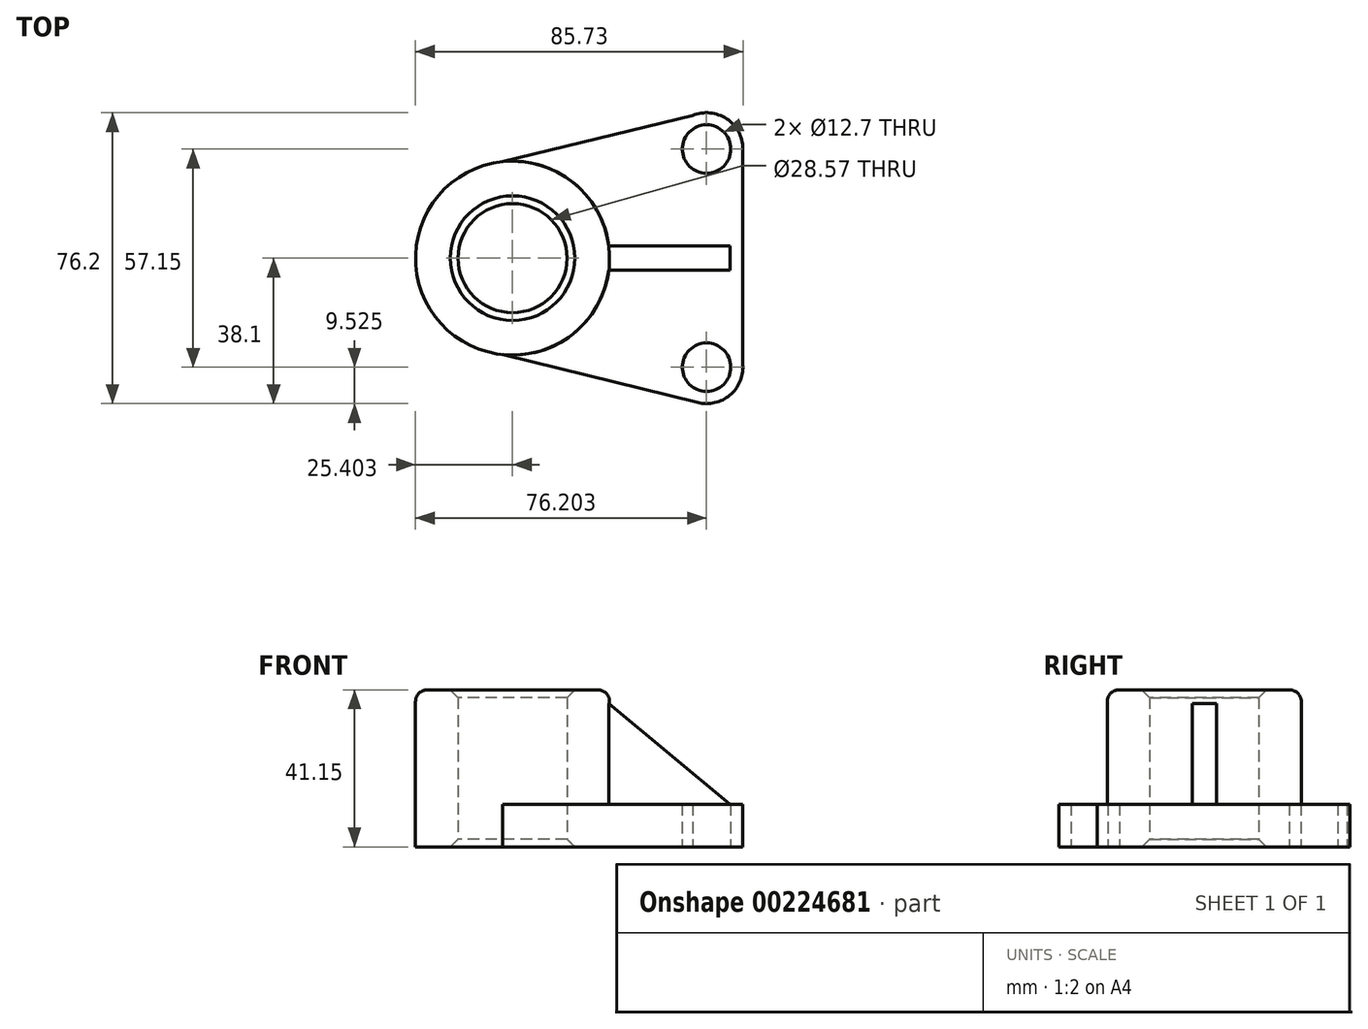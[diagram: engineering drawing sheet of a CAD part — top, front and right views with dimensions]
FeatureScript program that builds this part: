
annotation { "Feature Type Name" : "Feature", "Feature Type Description" : "" }
export const myFeature = defineFeature(function(context is Context, id is Id, definition is map)
    precondition{}
    {
        {
            var Q0;
            Q0=qCreatedBy(makeId("Top.planeOp"),FACE);
            var sketch = newSketch(context, id + "F0", { "sketchPlane" : qUnion([Q0])});
            skCircle(sketch, "E0", {"center": v(-42.43, 0) * mm, "radius": 25.4 * mm});
            skCircle(sketch, "E1", {"center": v(-42.43, 0) * mm, "radius": 14.29 * mm});
            skCircle(sketch, "E2", {"center": v(8.37, 28.58) * mm, "radius": 6.35 * mm});
            skCircle(sketch, "E3", {"center": v(8.37, -28.58) * mm, "radius": 6.35 * mm});
            skCircle(sketch, "E4", {"center": v(8.37, 28.58) * mm, "radius": 9.53 * mm});
            skCircle(sketch, "E5", {"center": v(8.37, -28.58) * mm, "radius": 9.53 * mm});
            skLineSegment(sketch, "E6", {"start": v(4.69, 37.36) * mm, "end": v(-45, 25.27) * mm});
            skLineSegment(sketch, "E7", {"start": v(17.88, -28.04) * mm, "end": v(17.9, 28.58) * mm});
            skLineSegment(sketch, "E8", {"start": v(-45, -25.27) * mm, "end": v(6.1, -37.82) * mm});
            skLineSegment(sketch, "E9.bottom", {"start": v(14.59, -3.18) * mm, "end": v(-23.83, -3.18) * mm});
            skLineSegment(sketch, "E9.top", {"start": v(14.59, 3.18) * mm, "end": v(-23.83, 3.18) * mm});
            skLineSegment(sketch, "E9.left", {"start": v(14.59, -3.18) * mm, "end": v(14.59, 3.18) * mm});
            skLineSegment(sketch, "E9.right", {"start": v(-23.83, -3.18) * mm, "end": v(-23.83, 3.18) * mm});
            skPoint(sketch, "E9.middle", {"position": v(-4.62, 0) * mm});
            skSolve(sketch);
        }
        {
            var Q0;
            Q0=makeQuery(id+"F0.imprint","IMPRINT",FACE,{"disambiguationData":[TD([[makeQuery(id+"F0.imprint","IMPRINT",EDGE,{"derivedFrom":sQuery(id+"F0.wireOp",EDGE,"E1")}),-1.0]])]});
            var Q1;
            {var subQ5=sQuery(id+"F0.wireOp",EDGE,"E9.right");Q1=makeQuery(id+"F0.imprint","IMPRINT",FACE,{"disambiguationData":[TD([[makeQuery(id+"F0.imprint","IMPRINT",EDGE,{"derivedFrom":subQ5}),-1.0]])]});}
            extrude(context, id + "F1", {"entities" : qUnion([Q0, Q1]), "depth" : 41.15 * mm});
        }
        {
            var Q0;
            {var subQ6=sQuery(id+"F0.wireOp",EDGE,"E6");Q0=makeQuery(id+"F0.imprint","IMPRINT",FACE,{"disambiguationData":[TD([[makeQuery(id+"F0.imprint","IMPRINT",EDGE,{"derivedFrom":subQ6}),1.0]])]});}
            var Q1;
            Q1=makeQuery(id+"F0.imprint","IMPRINT",FACE,{"disambiguationData":[TD([[makeQuery(id+"F0.imprint","IMPRINT",EDGE,{"derivedFrom":sQuery(id+"F0.wireOp",EDGE,"E2")}),1.0]])]});
            var Q2;
            Q2=makeQuery(id+"F0.imprint","IMPRINT",FACE,{"disambiguationData":[TD([[makeQuery(id+"F0.imprint","IMPRINT",EDGE,{"derivedFrom":sQuery(id+"F0.wireOp",EDGE,"E3")}),1.0]])]});
            var Q3;
            Q3=makeQuery(id+"F0.imprint","IMPRINT",FACE,{"disambiguationData":[TD([[makeQuery(id+"F0.imprint","IMPRINT",EDGE,{"derivedFrom":sQuery(id+"F0.wireOp",EDGE,"E3")}),-1.0]])]});
            var Q4;
            Q4=makeQuery(id+"F0.imprint","IMPRINT",FACE,{"disambiguationData":[TD([[makeQuery(id+"F0.imprint","IMPRINT",EDGE,{"derivedFrom":sQuery(id+"F0.wireOp",EDGE,"E2")}),-1.0]])]});
            var Q5;
            {var subQ5=sQuery(id+"F0.wireOp",EDGE,"E9.left");Q5=makeQuery(id+"F0.imprint","IMPRINT",FACE,{"disambiguationData":[TD([[makeQuery(id+"F0.imprint","IMPRINT",EDGE,{"derivedFrom":subQ5}),1.0]])]});}
            var Q6;
            {var subQ5=sQuery(id+"F0.wireOp",EDGE,"E9.right");Q6=makeQuery(id+"F0.imprint","IMPRINT",FACE,{"disambiguationData":[TD([[makeQuery(id+"F0.imprint","IMPRINT",EDGE,{"derivedFrom":subQ5}),-1.0]])]});}
            extrude(context, id + "F2", {"entities" : qUnion([Q0, Q1, Q2, Q3, Q4, Q5, Q6]), "operationType" : NewBodyOperationType.ADD, "depth" : 11.18 * mm});
        }
        {
            var Q0;
            {var subQ5=sQuery(id+"F0.wireOp",EDGE,"E9.left");Q0=makeQuery(id+"F0.imprint","IMPRINT",FACE,{"disambiguationData":[TD([[makeQuery(id+"F0.imprint","IMPRINT",EDGE,{"derivedFrom":subQ5}),1.0]])]});}
            extrude(context, id + "F3", {"entities" : qUnion([Q0]), "operationType" : NewBodyOperationType.ADD, "depth" : 37.6 * mm});
        }
        {
            var Q0;
            Q0=makeQuery(id+"F3.opExtrude","SWEPT_FACE",FACE,{"disambiguationData":[OSD([sQuery(id+"F0.wireOp",EDGE,"E9.bottom")])]});
            var sketch = newSketch(context, id + "F4", { "sketchPlane" : qUnion([Q0])});
            skLineSegment(sketch, "E10", {"start": v(-17.23, 37.6) * mm, "end": v(14.59, 11.18) * mm});
            skSolve(sketch);
        }
        {
            var Q0;
            Q0 = qSketchRegion(id + "F4", true);
            var Q1;
            Q1=makeQuery(id+"F4.imprint","IMPRINT",FACE,{"disambiguationData":[TD([[makeQuery(id+"F4.imprint","IMPRINT",EDGE,{"derivedFrom":sQuery(id+"F4.wireOp",EDGE,"E10")}),1.0]])]});
            extrude(context, id + "F5", {"entities" : qUnion([Q0, Q1]), "operationType" : NewBodyOperationType.REMOVE, "oppositeDirection" : true, "depth" : 127 * mm});
        }
        {
            var Q0;
            Q0=makeQuery(id+"F0.imprint","IMPRINT",FACE,{"disambiguationData":[TD([[makeQuery(id+"F0.imprint","IMPRINT",EDGE,{"derivedFrom":sQuery(id+"F0.wireOp",EDGE,"E2")}),1.0]])]});
            var Q1;
            Q1=makeQuery(id+"F0.imprint","IMPRINT",FACE,{"disambiguationData":[TD([[makeQuery(id+"F0.imprint","IMPRINT",EDGE,{"derivedFrom":sQuery(id+"F0.wireOp",EDGE,"E3")}),1.0]])]});
            extrude(context, id + "F6", {"entities" : qUnion([Q0, Q1]), "operationType" : NewBodyOperationType.REMOVE, "depth" : 76.2 * mm});
        }
        {
            var Q0;
            Q0=makeQuery(id+"F1.opExtrude","CAP_EDGE",EDGE,{"disambiguationData":[OSD([sQuery(id+"F0.wireOp",EDGE,"E0")])],"isStart":false});
            fillet(context, id + "F7", {"entities" : qUnion([Q0]), "radius" : 3.05 * mm, "tangentPropagation" : true, "allowEdgeOverflow" : false});
        }
        {
            var Q0;
            Q0=makeQuery(id+"F1.opExtrude","CAP_EDGE",EDGE,{"disambiguationData":[OSD([sQuery(id+"F0.wireOp",EDGE,"E1")])],"isStart":false});
            var Q1;
            Q1=makeQuery(id+"F1.opExtrude","CAP_FACE",FACE,{"disambiguationData":[OSD([sQuery(id+"F0.wireOp",EDGE,"E0"),sQuery(id+"F0.wireOp",EDGE,"E1")])],"isStart":false});
            chamfer(context, id + "F8", {"entities" : qUnion([Q0, Q1]), "chamferType" : ChamferType.OFFSET_ANGLE, "width" : 2.03 * mm, "oppositeDirection" : false, "angle" : 45 * degree, "tangentPropagation" : true});
        }
        {
            var Q0;
            Q0=makeQuery(id+"F1.opExtrude","CAP_EDGE",EDGE,{"disambiguationData":[OSD([sQuery(id+"F0.wireOp",EDGE,"E1")])],"isStart":true});
            chamfer(context, id + "F9", {"entities" : qUnion([Q0]), "chamferType" : ChamferType.OFFSET_ANGLE, "width" : 2.03 * mm, "oppositeDirection" : false, "angle" : 45 * degree, "tangentPropagation" : true});
        }
    });
